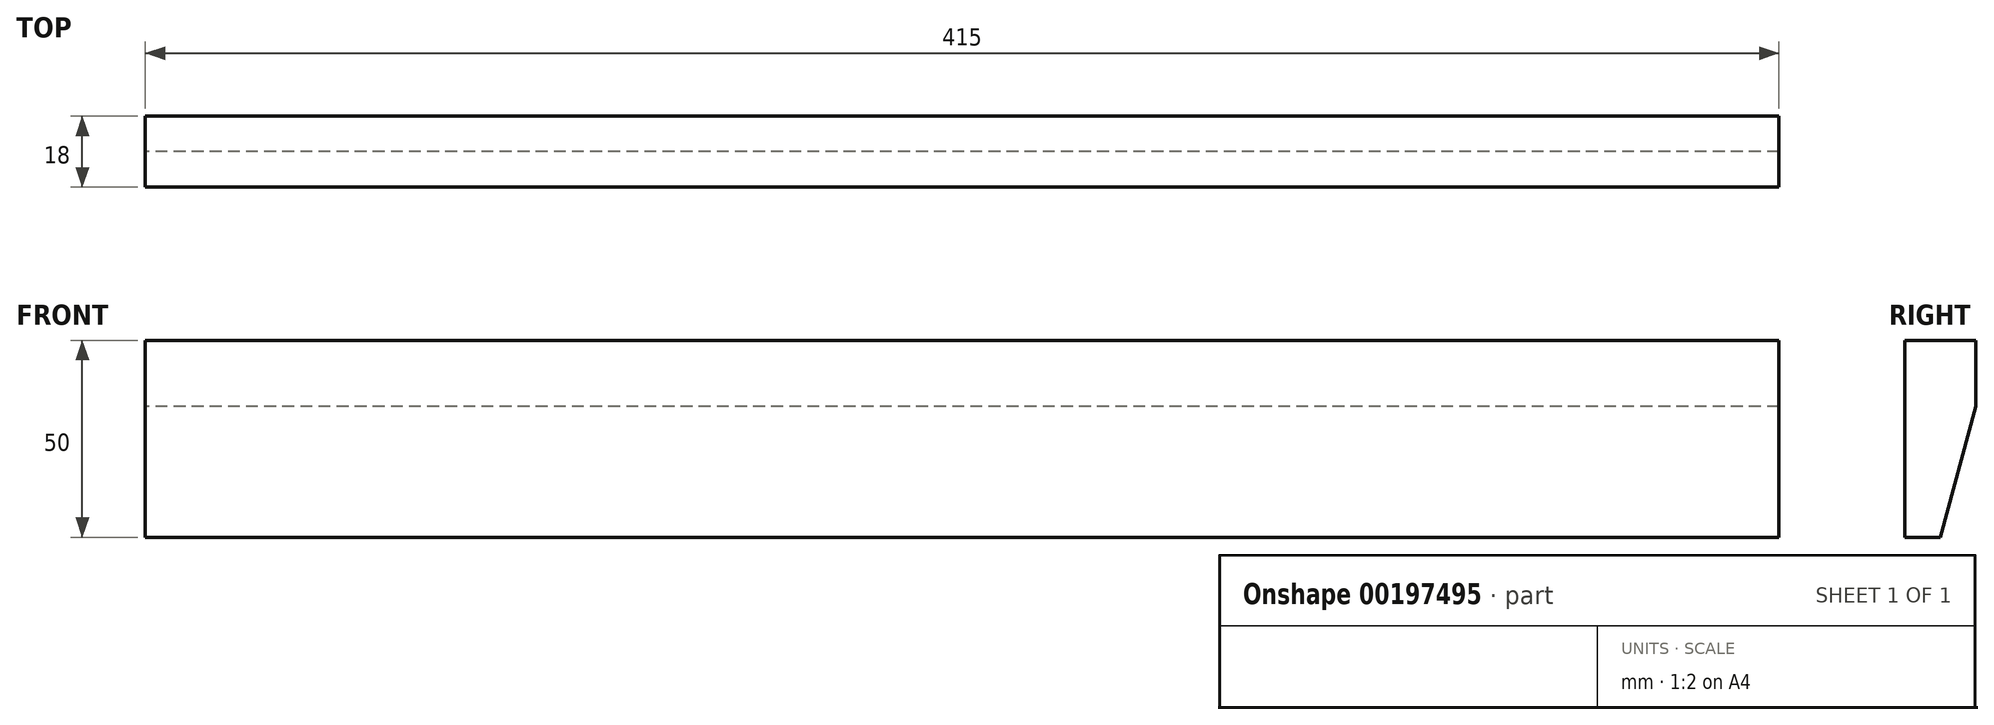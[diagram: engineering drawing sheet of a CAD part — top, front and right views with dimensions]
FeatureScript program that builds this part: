
annotation { "Feature Type Name" : "Feature", "Feature Type Description" : "" }
export const myFeature = defineFeature(function(context is Context, id is Id, definition is map)
    precondition{}
    {
        {
            var Q0;
            Q0=qCreatedBy(makeId("Right.planeOp"),FACE);
            var sketch = newSketch(context, id + "F0", { "sketchPlane" : qUnion([Q0])});
            skLineSegment(sketch, "E0.bottom", {"start": v(-9, 25) * mm, "end": v(9, 25) * mm});
            skLineSegment(sketch, "E0.top", {"start": v(-9, -25) * mm, "end": v(0, -25) * mm});
            skLineSegment(sketch, "E0.left", {"start": v(-9, 25) * mm, "end": v(-9, -25) * mm});
            skLineSegment(sketch, "E0.right", {"start": v(9, 25) * mm, "end": v(9, 8.25) * mm});
            skPoint(sketch, "E0.middle", {"position": v(0, 0) * mm});
            skLineSegment(sketch, "E1", {"start": v(0, -25) * mm, "end": v(9, 8.25) * mm});
            skPoint(sketch, "E2.orphan", {"position": v(9, -25) * mm});
            skSolve(sketch);
        }
        {
            var Q0;
            Q0 = qSketchRegion(id + "F0", true);
            extrude(context, id + "F1", {"entities" : qUnion([Q0]), "depth" : 415 * mm});
        }
    });
